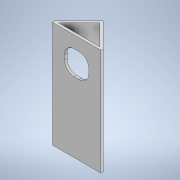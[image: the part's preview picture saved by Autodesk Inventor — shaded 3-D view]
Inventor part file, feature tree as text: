
AUTODESK INVENTOR PART (.ipt)
format: ipt  version: 2020 (Build 240168000, 168)  size: 138,240 bytes
history: native  units: mm
features: extrude x3, sketch x3
ambient origin geometry x8: Origin, YZ Plane, XZ Plane, XY Plane, X Axis, Y Axis, Z Axis, Center Point
bodies: Solid1 (feature_tree)
feature tree (6):
  extrude  "Extrusion1"  Depth=220.0mm
  extrude  "Extrusion2"  TaperAngle=45.0deg  [1 undecoded]
  extrude  "Extrusion5"  Depth=5.0mm
  sketch  "Sketch1"  dims[d0=100.0mm d1=220.0mm]
  sketch  "Sketch2"  dims[d2=5.0mm d3=0.0mm d4=45.0deg]
  sketch  "Sketch5"  dims[d5=5.0mm d6=5.0mm d7=45.0mm d8=0.0mm d16=50.0mm d17=50.0mm d18=20.0mm d19=5.0mm d20=0.0mm]
note: 1 required parameter value undecoded (feature->parameter linkage not recoverable at this tier; creation-order binding heuristic only, values carry confidence <= 0.55)
